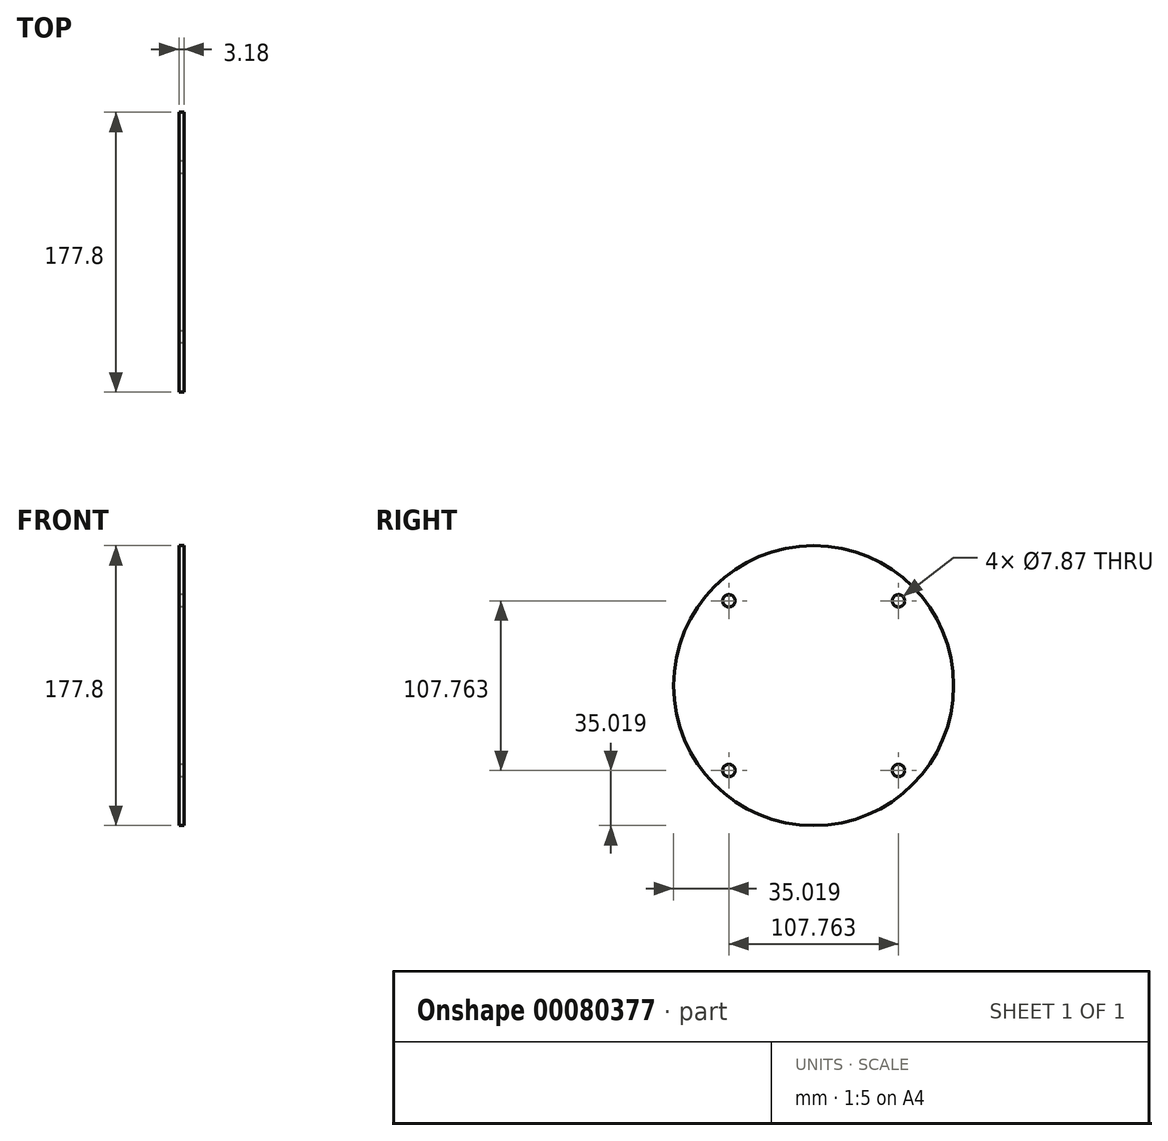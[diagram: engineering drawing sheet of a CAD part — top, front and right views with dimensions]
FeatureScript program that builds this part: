
annotation { "Feature Type Name" : "Feature", "Feature Type Description" : "" }
export const myFeature = defineFeature(function(context is Context, id is Id, definition is map)
    precondition{}
    {
        {
            var Q0;
            Q0=qCreatedBy(makeId("Right.planeOp"),FACE);
            var sketch = newSketch(context, id + "F0", { "sketchPlane" : qUnion([Q0])});
            skCircle(sketch, "E0", {"center": v(0, 0) * mm, "radius": 88.9 * mm});
            skCircle(sketch, "E1", {"center": v(0, 0) * mm, "radius": 76.2 * mm, "construction": true});
            skLineSegment(sketch, "E2", {"start": v(0, 0) * mm, "end": v(0, 114.77) * mm, "construction": true});
            skLineSegment(sketch, "E3", {"start": v(0, 0) * mm, "end": v(-92.26, 92.26) * mm, "construction": true});
            skCircle(sketch, "E4", {"center": v(-53.88, 53.88) * mm, "radius": 3.94 * mm});
            skCircle(sketch, "E5.1.0", {"center": v(-53.88, -53.88) * mm, "radius": 3.94 * mm});
            skCircle(sketch, "E5.2.0", {"center": v(53.88, -53.88) * mm, "radius": 3.94 * mm});
            skCircle(sketch, "E5.3.0", {"center": v(53.88, 53.88) * mm, "radius": 3.94 * mm});
            skSolve(sketch);
        }
        {
            var Q0;
            Q0 = qSketchRegion(id + "F0", true);
            extrude(context, id + "F1", {"entities" : qUnion([Q0]), "depth" : 3.17 * mm});
        }
    });
